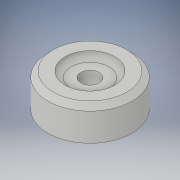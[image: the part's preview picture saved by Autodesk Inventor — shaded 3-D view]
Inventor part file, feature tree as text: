
AUTODESK INVENTOR PART (.ipt)
format: ipt  version: 2018 (Build 220112000, 112)  size: 146,432 bytes
history: native  units: in
note: dims shown in document units (in); Inventor stores cm internally (conversion verified against a paired STEP export)
features: sketch x3, revolve x2, extrude x1, chamfer x1
ambient origin geometry x8: Origin, YZ Plane, XZ Plane, XY Plane, X Axis, Y Axis, Z Axis, Center Point
bodies: Solid1 (feature_tree)
feature tree (7):
  revolve  "Revolution1"  Angle=45.0deg
  revolve  "Revolution3"  [1 undecoded]
  extrude  "Extrusion4"  TaperAngle=90.0deg  [1 undecoded]
  chamfer  "Chamfer3"  Distance=0.115in
  sketch  "Sketch1"  dims[d0=0.125in d5=45.0deg]
  sketch  "Sketch8"  dims[d6=0.0625in d7=0.125in]
  sketch  "Sketch9"  dims[d8=0.25in d9=90.0deg d14=0.115in d31=0.139in d32=0.1562in d33=90.0deg d34=0.2188in d35=0.0695in d36=0.0in d37=0.5in d38=0.0625in d39=0.125in d40=45.0deg]
note: 2 required parameter values undecoded (feature->parameter linkage not recoverable at this tier; creation-order binding heuristic only, values carry confidence <= 0.55)